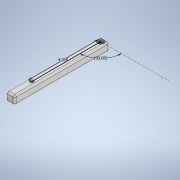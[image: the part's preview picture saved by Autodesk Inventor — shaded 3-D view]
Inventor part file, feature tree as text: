
AUTODESK INVENTOR PART (.ipt)
format: ipt  version: 2020 (Build 240168000, 168)  size: 163,328 bytes
history: native  units: in
note: dims shown in document units (in); Inventor stores cm internally (conversion verified against a paired STEP export)
features: sketch x5, extrude x3, hole x3, fillet x1
ambient origin geometry x8: Origin, YZ Plane, XZ Plane, XY Plane, X Axis, Y Axis, Z Axis, Center Point
bodies: Solid1 (feature_tree)
feature tree (12):
  extrude  "Extrusion1"  Depth=0.5in
  extrude  "Extrusion2"  Depth=0.5in TaperAngle=0.0deg
  extrude  "Extrusion3"  Depth=0.25in
  fillet  "Fillet1"  Radius=0.175in
  sketch  "Sketch4"  dims[d9=5.0in d10=0.0in d11=0.1in]
  hole  "Hole1"  [1 undecoded]
  hole  "Hole2"  [1 undecoded]
  hole  "Hole3"  [1 undecoded]
  sketch  "Sketch1"  dims[d0=0.5in d1=0.5in]
  sketch  "Sketch2"  dims[d2=0.375in d3=0.5in d4=0.0in]
  sketch  "Sketch3"  dims[d5=0.25in d6=0.125in d7=0.175in d8=0.0in]
  sketch  "Sketch5"  dims[d12=4.01in d13=90.0deg d14=0.213in d15=0.75in d16=0.438in d17=0.25in d18=0.5635in d19=0.25in d20=0.0in d21=0.125in d22=0.75in d23=0.438in d24=0.25in d25=0.5635in d26=1.0in d27=0.8108in d28=3.66in d29=0.0in d30=0.25in d31=90.0deg d32=0.213in d33=0.75in d34=0.438in d35=0.25in d36=0.5635in d37=0.25in d38=0.0in]
note: 3 required parameter values undecoded (feature->parameter linkage not recoverable at this tier; creation-order binding heuristic only, values carry confidence <= 0.55)
